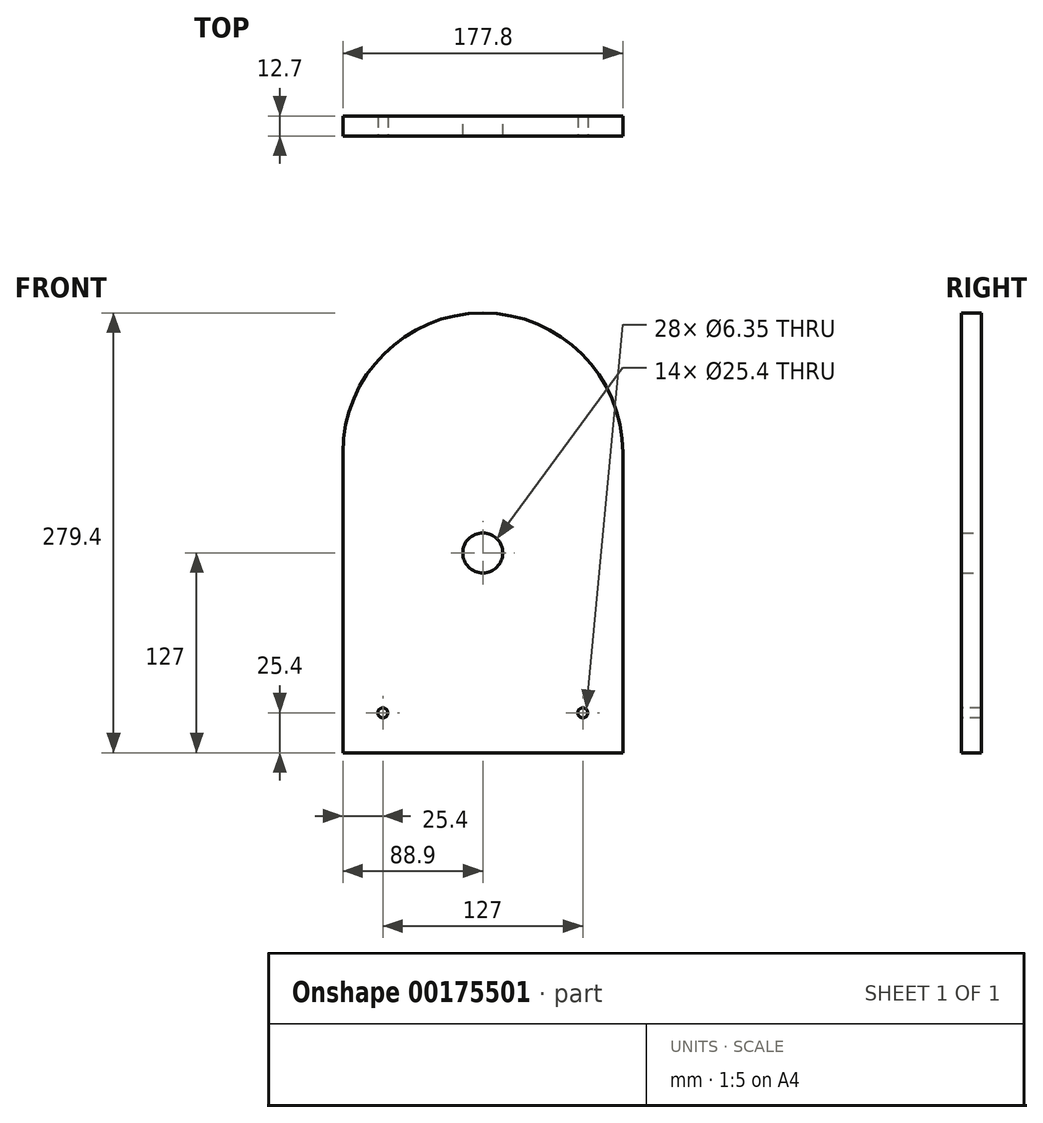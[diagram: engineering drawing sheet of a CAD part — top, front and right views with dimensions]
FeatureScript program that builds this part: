
annotation { "Feature Type Name" : "Feature", "Feature Type Description" : "" }
export const myFeature = defineFeature(function(context is Context, id is Id, definition is map)
    precondition{}
    {
        {
            var Q0;
            Q0=qCreatedBy(makeId("Front.planeOp"),FACE);
            var sketch = newSketch(context, id + "F0", { "sketchPlane" : qUnion([Q0])});
            skLineSegment(sketch, "E0.bottom", {"start": v(0, 139.7) * mm, "end": v(0, 139.7) * mm});
            skLineSegment(sketch, "E0.top", {"start": v(88.9, -139.7) * mm, "end": v(-88.9, -139.7) * mm});
            skLineSegment(sketch, "E0.left", {"start": v(88.9, 50.8) * mm, "end": v(88.9, -139.7) * mm});
            skLineSegment(sketch, "E0.right", {"start": v(-88.9, 50.8) * mm, "end": v(-88.9, -139.7) * mm});
            skPoint(sketch, "E0.middle", {"position": v(0, 0) * mm});
            skLineSegment(sketch, "E1", {"start": v(0, -139.7) * mm, "end": v(0, -12.7) * mm});
            skPoint(sketch, "E1.endSnap0", {"position": v(0, -139.7) * mm});
            skCircle(sketch, "E2", {"center": v(0, -12.7) * mm, "radius": 12.7 * mm});
            skPoint(sketch, "E3.visualSharp", {"position": v(-88.9, 139.7) * mm});
            skArc(sketch, "E3.filletArc", {"start": v(0, 139.7) * mm, "mid": v(-62.86, 113.66) * mm, "end": v(-88.9, 50.8) * mm});
            skPoint(sketch, "E4.visualSharp", {"position": v(88.9, 139.7) * mm});
            skArc(sketch, "E4.filletArc", {"start": v(88.9, 50.8) * mm, "mid": v(62.86, 113.66) * mm, "end": v(0, 139.7) * mm});
            skSolve(sketch);
        }
        {
            var Q0;
            Q0 = qSketchRegion(id + "F0", true);
            extrude(context, id + "F1", {"entities" : qUnion([Q0]), "depth" : 12.7 * mm});
        }
        {
            var Q0;
            Q0=makeQuery(id+"F1.opExtrude","CAP_FACE",FACE,{"disambiguationData":[OSD([sQuery(id+"F0.wireOp",EDGE,"E0.top"),sQuery(id+"F0.wireOp",EDGE,"E0.left"),sQuery(id+"F0.wireOp",EDGE,"E0.right"),sQuery(id+"F0.wireOp",EDGE,"E2"),sQuery(id+"F0.wireOp",EDGE,"E3.filletArc"),sQuery(id+"F0.wireOp",EDGE,"E4.filletArc")])],"isStart":false});
            var sketch = newSketch(context, id + "F2", { "sketchPlane" : qUnion([Q0])});
            skLineSegment(sketch, "E5", {"start": v(-88.9, -139.7) * mm, "end": v(-88.9, -114.3) * mm});
            skLineSegment(sketch, "E6", {"start": v(-88.9, -114.3) * mm, "end": v(-63.5, -114.3) * mm});
            skLineSegment(sketch, "E7", {"start": v(88.9, -139.7) * mm, "end": v(88.9, -114.3) * mm});
            skLineSegment(sketch, "E8", {"start": v(88.9, -114.3) * mm, "end": v(63.5, -114.3) * mm});
            skCircle(sketch, "E9", {"center": v(-63.5, -114.3) * mm, "radius": 3.18 * mm});
            skCircle(sketch, "E10", {"center": v(63.5, -114.3) * mm, "radius": 3.18 * mm});
            skSolve(sketch);
        }
        {
            var Q0;
            Q0 = qSketchRegion(id + "F2", true);
            extrude(context, id + "F3", {"entities" : qUnion([Q0]), "operationType" : NewBodyOperationType.REMOVE, "endBound" : BoundingType.THROUGH_ALL, "oppositeDirection" : true, "depth" : 25.4 * mm});
        }
    });
